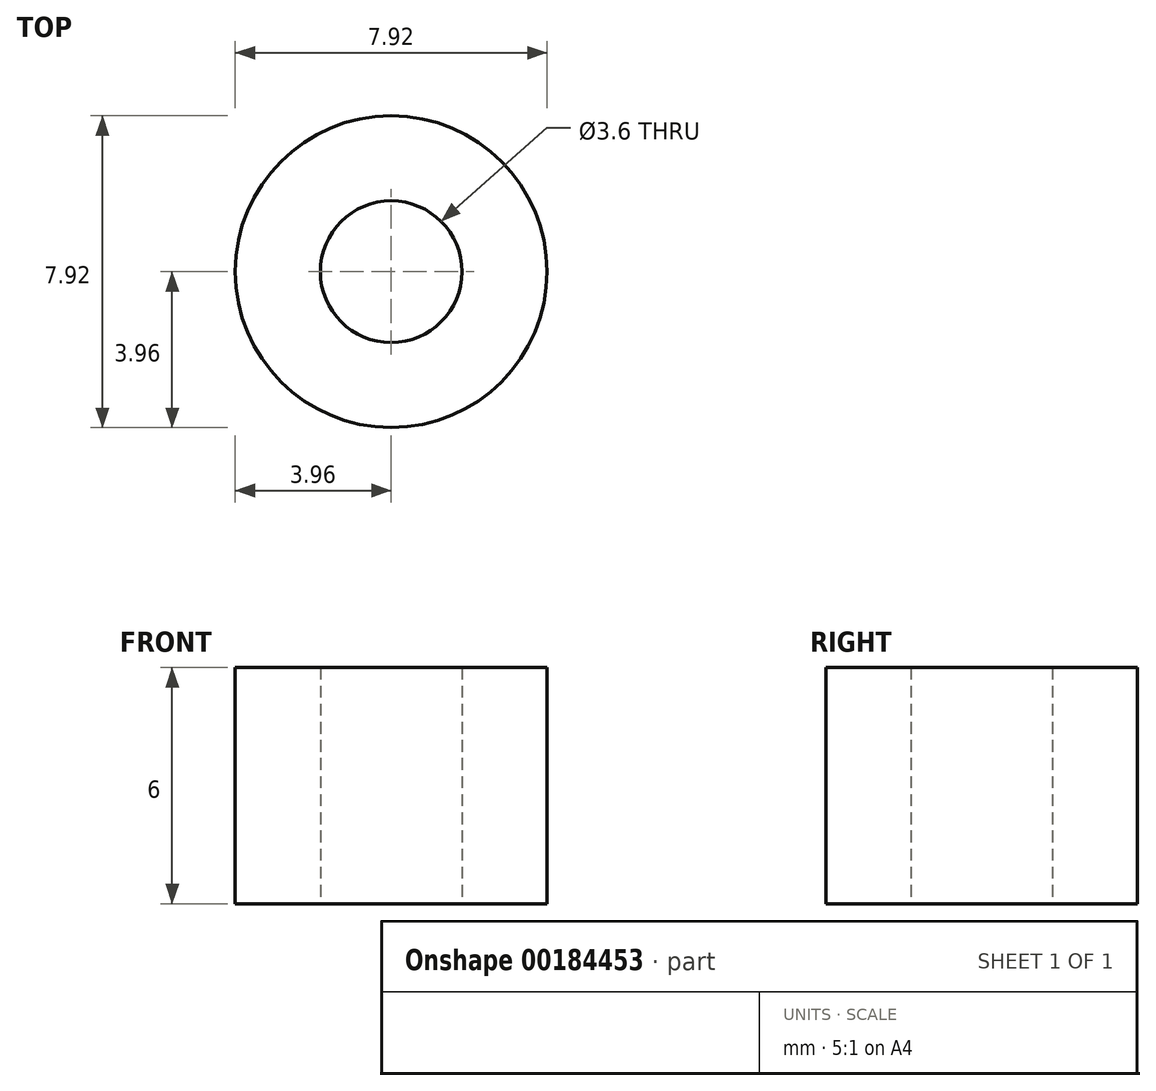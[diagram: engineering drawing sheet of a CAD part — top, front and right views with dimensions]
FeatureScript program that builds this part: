
annotation { "Feature Type Name" : "Feature", "Feature Type Description" : "" }
export const myFeature = defineFeature(function(context is Context, id is Id, definition is map)
    precondition{}
    {
        {
            var Q0;
            Q0=qCreatedBy(makeId("Top.planeOp"),FACE);
            var sketch = newSketch(context, id + "F0", { "sketchPlane" : qUnion([Q0])});
            skCircle(sketch, "E0", {"center": v(0, 0) * mm, "radius": 3.96 * mm});
            skCircle(sketch, "E1", {"center": v(0, 0) * mm, "radius": 1.8 * mm});
            skSolve(sketch);
        }
        {
            var Q0;
            Q0=makeQuery(id+"F0.imprint","IMPRINT",FACE,{"disambiguationData":[TD([[makeQuery(id+"F0.imprint","IMPRINT",EDGE,{"derivedFrom":sQuery(id+"F0.wireOp",EDGE,"E0")}),1.0]])]});
            extrude(context, id + "F1", {"entities" : qUnion([Q0]), "depth" : 6 * mm});
        }
    });
